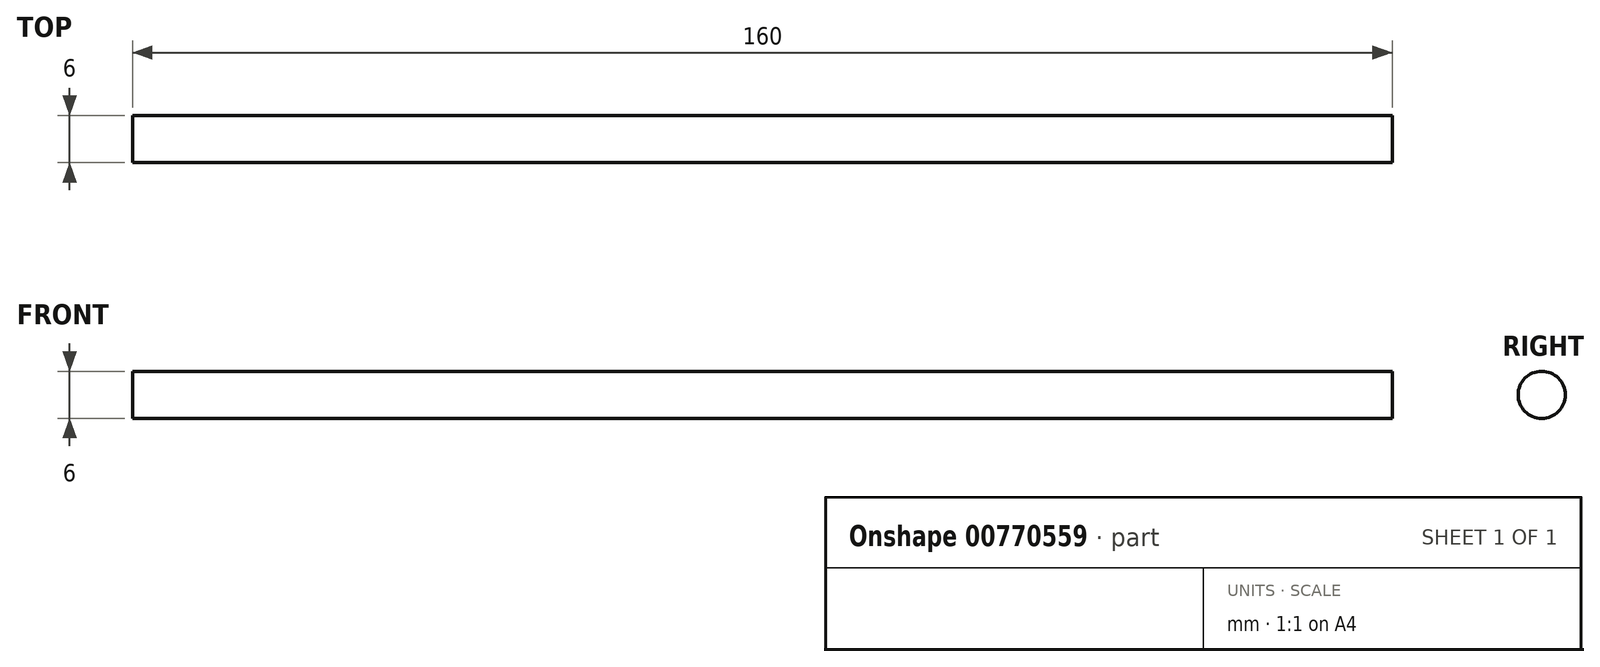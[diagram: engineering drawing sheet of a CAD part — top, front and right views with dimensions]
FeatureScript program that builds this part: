
annotation { "Feature Type Name" : "Feature", "Feature Type Description" : "" }
export const myFeature = defineFeature(function(context is Context, id is Id, definition is map)
    precondition{}
    {
        {
            var Q0;
            Q0=qCreatedBy(makeId("Right.planeOp"),FACE);
            var sketch = newSketch(context, id + "F0", { "sketchPlane" : qUnion([Q0])});
            skCircle(sketch, "E0", {"center": v(0, 0) * mm, "radius": 3 * mm});
            skSolve(sketch);
        }
        {
            var Q0;
            Q0 = qSketchRegion(id + "F0", true);
            extrude(context, id + "F1", {"entities" : qUnion([Q0]), "depth" : 160 * mm, "offsetDistance" : 25 * mm});
        }
    });
